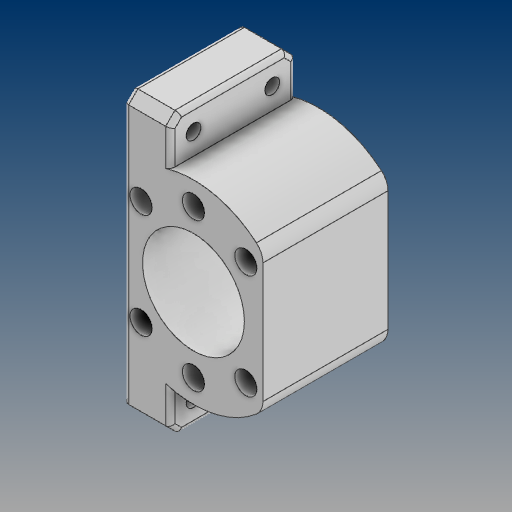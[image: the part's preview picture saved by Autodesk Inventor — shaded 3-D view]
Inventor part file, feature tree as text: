
AUTODESK INVENTOR PART (.ipt)
format: ipt  version: 2021 (Build 250183000, 183)  size: 240,128 bytes
history: native  units: mm
features: sketch x3, fillet x3, projected_geometry x3, extrude x2, reference x2, other x2, plane x1, hole x1, chamfer x1
ambient origin geometry x8: Origin, YZ Plane, XZ Plane, XY Plane, X Axis, Y Axis, Z Axis, Center Point
bodies: Solid1 (feature_tree)
feature tree (18):
  sketch  "Sketch1"  dims[d0=30.0mm d1=60.0mm]
  plane  "Work Plane1"
  extrude  "Extrusion1"  Depth=60.0mm
  hole  "Hole1"  [1 undecoded]
  extrude  "Extrusion2"  Depth=1.0mm
  chamfer  "Chamfer1"  Distance=5.0mm
  fillet  "Fillet1"  Radius=10.0mm
  fillet  "Fillet2"  [1 undecoded]
  fillet  "Fillet3"  Radius=2.0mm
  reference  "Reference1"
  sketch  "Sketch2"  dims[d2=30.0mm d3=21.0mm]
  projected_geometry  "Projected Loop1"
  projected_geometry  "Projected Loop2"
  sketch  "Sketch3"  dims[d4=30.5mm d5=0.0mm d7=5.0mm d9=5.0mm d10=3.2mm d11=6.0mm d12=4.0mm d13=2.0mm d14=90.0deg d15=8.0mm d16=20.594885mm d17=10.0mm d18=0.0mm d19=0.0mm d20=2.0mm d21=2.0mm d22=45.0deg d23=4.0mm d24=1.0mm d25=1.0mm]
  reference  "Reference2"
  projected_geometry  "Projected Loop3"
  other  "Assembly1"
  other  "1204 BALL NUT:1"
note: 2 required parameter values undecoded (feature->parameter linkage not recoverable at this tier; creation-order binding heuristic only, values carry confidence <= 0.55)
